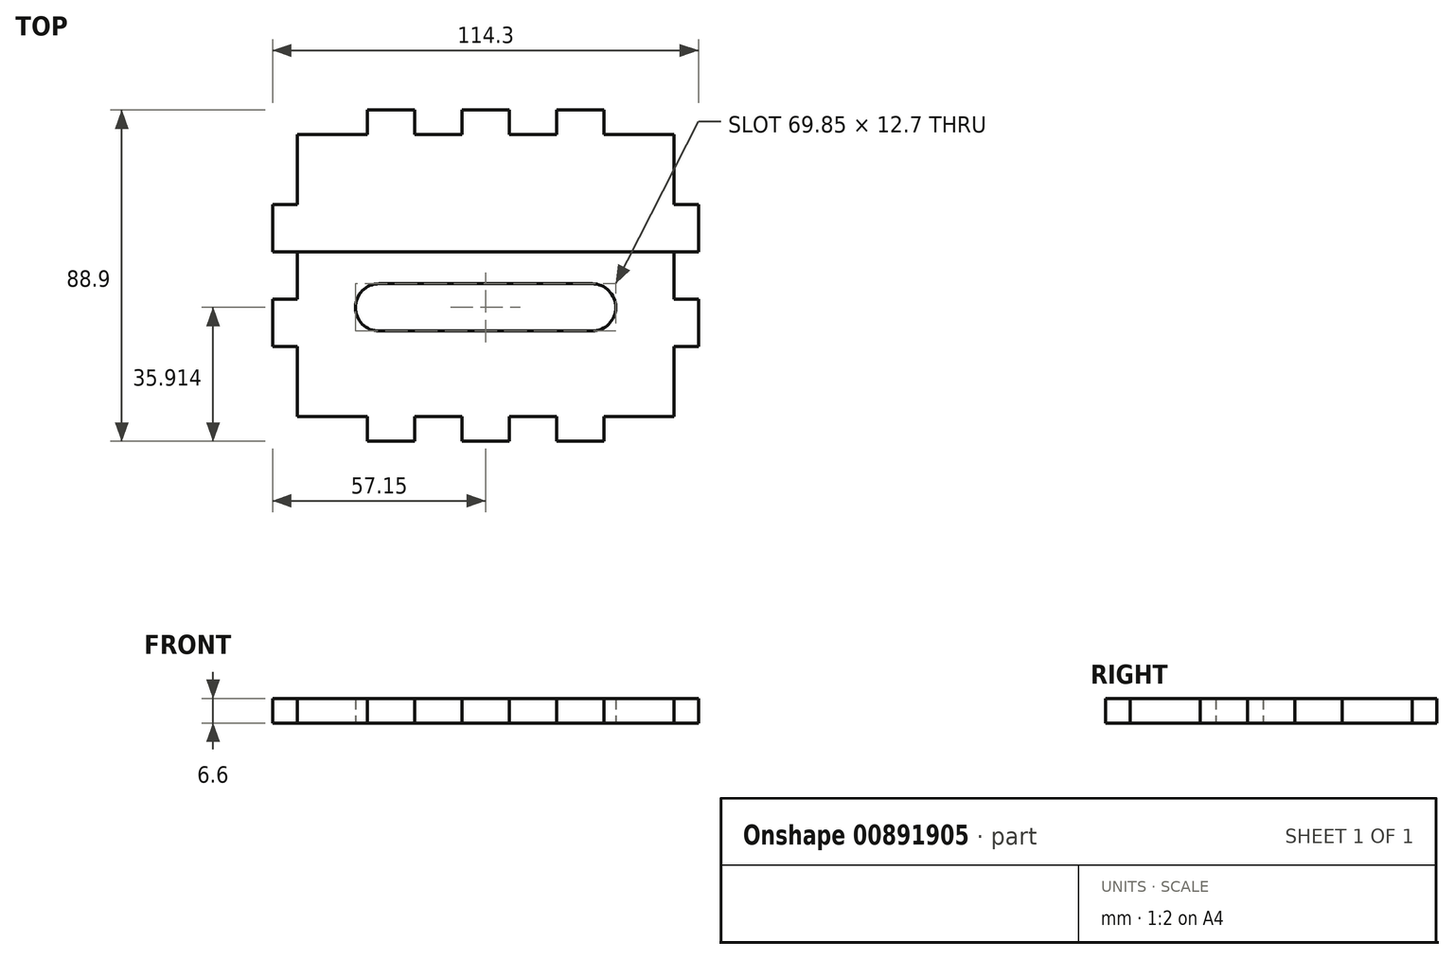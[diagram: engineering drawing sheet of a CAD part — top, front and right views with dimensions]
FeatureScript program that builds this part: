
annotation { "Feature Type Name" : "Feature", "Feature Type Description" : "" }
export const myFeature = defineFeature(function(context is Context, id is Id, definition is map)
    precondition{}
    {
        {
            var Q0;
            Q0=qCreatedBy(makeId("Top.planeOp"),FACE);
            var sketch = newSketch(context, id + "F0", { "sketchPlane" : qUnion([Q0])});
            skLineSegment(sketch, "E0.bottom", {"start": v(25.4, 0) * mm, "end": v(38.1, 0) * mm});
            skLineSegment(sketch, "E0.left", {"start": v(0, -25.4) * mm, "end": v(0, -38.1) * mm});
            skLineSegment(sketch, "E1", {"start": v(6.6, -6.6) * mm, "end": v(25.4, -6.6) * mm});
            skLineSegment(sketch, "E2", {"start": v(25.4, -6.6) * mm, "end": v(25.4, 0) * mm});
            skLineSegment(sketch, "E3", {"start": v(38.1, 0) * mm, "end": v(38.1, -6.6) * mm});
            skLineSegment(sketch, "E4", {"start": v(38.1, -6.6) * mm, "end": v(50.8, -6.6) * mm});
            skLineSegment(sketch, "E5", {"start": v(50.8, -6.6) * mm, "end": v(50.8, 0) * mm});
            skLineSegment(sketch, "E6", {"start": v(50.8, 0) * mm, "end": v(63.5, 0) * mm});
            skLineSegment(sketch, "E7", {"start": v(63.5, 0) * mm, "end": v(63.5, -6.6) * mm});
            skLineSegment(sketch, "E8", {"start": v(63.5, -6.6) * mm, "end": v(76.2, -6.6) * mm});
            skLineSegment(sketch, "E9", {"start": v(76.2, -6.6) * mm, "end": v(76.2, 0) * mm});
            skLineSegment(sketch, "E10", {"start": v(76.2, 0) * mm, "end": v(88.9, 0) * mm});
            skLineSegment(sketch, "E11", {"start": v(88.9, 0) * mm, "end": v(88.9, -6.6) * mm});
            skLineSegment(sketch, "E12", {"start": v(88.9, -6.6) * mm, "end": v(107.7, -6.6) * mm});
            skPoint(sketch, "E13.orphan", {"position": v(0, 0) * mm});
            skPoint(sketch, "E14.orphan", {"position": v(114.3, 0) * mm});
            skLineSegment(sketch, "E15", {"start": v(6.6, -6.6) * mm, "end": v(6.6, -25.4) * mm});
            skLineSegment(sketch, "E16", {"start": v(6.6, -25.4) * mm, "end": v(0, -25.4) * mm});
            skLineSegment(sketch, "E17", {"start": v(0, -38.1) * mm, "end": v(6.6, -38.1) * mm});
            skLineSegment(sketch, "E18", {"start": v(6.6, -38.1) * mm, "end": v(6.6, -50.8) * mm});
            skLineSegment(sketch, "E19", {"start": v(6.6, -50.8) * mm, "end": v(0, -50.8) * mm});
            skLineSegment(sketch, "E20", {"start": v(0, -50.8) * mm, "end": v(0, -63.5) * mm});
            skLineSegment(sketch, "E21", {"start": v(0, -63.5) * mm, "end": v(6.6, -63.5) * mm});
            skLineSegment(sketch, "E22", {"start": v(6.6, -63.5) * mm, "end": v(6.6, -82.3) * mm});
            skPoint(sketch, "E23.orphan", {"position": v(0, -6.6) * mm});
            skPoint(sketch, "E24.orphan", {"position": v(0, -88.9) * mm});
            skLineSegment(sketch, "E25", {"start": v(57.15, 0) * mm, "end": v(57.15, 0) * mm});
            skPoint(sketch, "E25.endSnap0", {"position": v(57.15, 0) * mm});
            skLineSegment(sketch, "E26", {"start": v(6.6, -44.45) * mm, "end": v(6.6, -44.45) * mm});
            skLineSegment(sketch, "E27.MirrorCS", {"start": v(107.7, -6.6) * mm, "end": v(107.7, -25.4) * mm});
            skLineSegment(sketch, "E28.MirrorCS", {"start": v(107.7, -25.4) * mm, "end": v(114.3, -25.4) * mm});
            skLineSegment(sketch, "E29.MirrorCS", {"start": v(114.3, -25.4) * mm, "end": v(114.3, -38.1) * mm});
            skLineSegment(sketch, "E30.MirrorCS", {"start": v(114.3, -38.1) * mm, "end": v(107.7, -38.1) * mm});
            skLineSegment(sketch, "E31.MirrorCS", {"start": v(107.7, -38.1) * mm, "end": v(107.7, -50.8) * mm});
            skLineSegment(sketch, "E32.MirrorCS", {"start": v(107.7, -50.8) * mm, "end": v(114.3, -50.8) * mm});
            skLineSegment(sketch, "E33.MirrorCS", {"start": v(114.3, -50.8) * mm, "end": v(114.3, -63.5) * mm});
            skLineSegment(sketch, "E34.MirrorCS", {"start": v(114.3, -63.5) * mm, "end": v(107.7, -63.5) * mm});
            skLineSegment(sketch, "E35.MirrorCS", {"start": v(107.7, -63.5) * mm, "end": v(107.7, -82.3) * mm});
            skLineSegment(sketch, "E36.MirrorCS", {"start": v(6.6, -82.3) * mm, "end": v(25.4, -82.3) * mm});
            skLineSegment(sketch, "E37.MirrorCS", {"start": v(25.4, -82.3) * mm, "end": v(25.4, -88.9) * mm});
            skLineSegment(sketch, "E38.MirrorCS", {"start": v(25.4, -88.9) * mm, "end": v(38.1, -88.9) * mm});
            skLineSegment(sketch, "E39.MirrorCS", {"start": v(38.1, -88.9) * mm, "end": v(38.1, -82.3) * mm});
            skLineSegment(sketch, "E40.MirrorCS", {"start": v(38.1, -82.3) * mm, "end": v(50.8, -82.3) * mm});
            skLineSegment(sketch, "E41.MirrorCS", {"start": v(50.8, -82.3) * mm, "end": v(50.8, -88.9) * mm});
            skLineSegment(sketch, "E42.MirrorCS", {"start": v(50.8, -88.9) * mm, "end": v(63.5, -88.9) * mm});
            skLineSegment(sketch, "E43.MirrorCS", {"start": v(63.5, -88.9) * mm, "end": v(63.5, -82.3) * mm});
            skLineSegment(sketch, "E44.MirrorCS", {"start": v(63.5, -82.3) * mm, "end": v(76.2, -82.3) * mm});
            skLineSegment(sketch, "E45.MirrorCS", {"start": v(76.2, -82.3) * mm, "end": v(76.2, -88.9) * mm});
            skLineSegment(sketch, "E46.MirrorCS", {"start": v(76.2, -88.9) * mm, "end": v(88.9, -88.9) * mm});
            skLineSegment(sketch, "E47.MirrorCS", {"start": v(88.9, -88.9) * mm, "end": v(88.9, -82.3) * mm});
            skLineSegment(sketch, "E48.MirrorCS", {"start": v(88.9, -82.3) * mm, "end": v(107.7, -82.3) * mm});
            skLineSegment(sketch, "E49", {"start": v(6.6, -38.1) * mm, "end": v(107.7, -38.1) * mm});
            skLineSegment(sketch, "E50.bottom", {"start": v(28.57, -46.64) * mm, "end": v(85.73, -46.64) * mm});
            skLineSegment(sketch, "E50.top", {"start": v(28.58, -59.34) * mm, "end": v(85.73, -59.34) * mm});
            skLineSegment(sketch, "E50.left", {"start": v(22.22, -52.99) * mm, "end": v(22.22, -52.99) * mm});
            skLineSegment(sketch, "E50.right", {"start": v(92.08, -52.99) * mm, "end": v(92.08, -52.99) * mm});
            skPoint(sketch, "E51.visualSharp", {"position": v(22.22, -46.64) * mm});
            skArc(sketch, "E51.filletArc", {"start": v(28.57, -46.64) * mm, "mid": v(24.08, -48.5) * mm, "end": v(22.22, -52.99) * mm});
            skPoint(sketch, "E52.visualSharp", {"position": v(22.22, -59.34) * mm});
            skArc(sketch, "E52.filletArc", {"start": v(22.22, -52.99) * mm, "mid": v(24.08, -57.48) * mm, "end": v(28.58, -59.34) * mm});
            skPoint(sketch, "E53.visualSharp", {"position": v(92.08, -59.34) * mm});
            skArc(sketch, "E53.filletArc", {"start": v(85.73, -59.34) * mm, "mid": v(90.22, -57.48) * mm, "end": v(92.07, -52.99) * mm});
            skPoint(sketch, "E54.visualSharp", {"position": v(92.08, -46.64) * mm});
            skArc(sketch, "E54.filletArc", {"start": v(92.08, -52.99) * mm, "mid": v(90.22, -48.5) * mm, "end": v(85.73, -46.64) * mm});
            skLineSegment(sketch, "E55", {"start": v(57.15, -46.64) * mm, "end": v(57.15, -38.1) * mm, "construction": true});
            skSolve(sketch);
        }
        {
            var Q0;
            Q0=makeQuery(id+"F0.imprint","IMPRINT",FACE,{"disambiguationData":[TD([[makeQuery(id+"F0.imprint","IMPRINT",EDGE,{"derivedFrom":sQuery(id+"F0.wireOp",EDGE,"E1")}),-1.0]])]});
            extrude(context, id + "F1", {"entities" : qUnion([Q0]), "depth" : 6.6 * mm, "offsetDistance" : 25.4 * mm});
        }
        {
            var Q0;
            Q0=makeQuery(id+"F0.imprint","IMPRINT",FACE,{"disambiguationData":[TD([[makeQuery(id+"F0.imprint","IMPRINT",EDGE,{"derivedFrom":sQuery(id+"F0.wireOp",EDGE,"E18")}),1.0]])]});
            extrude(context, id + "F2", {"entities" : qUnion([Q0]), "depth" : 6.6 * mm, "offsetDistance" : 25.4 * mm});
        }
    });
